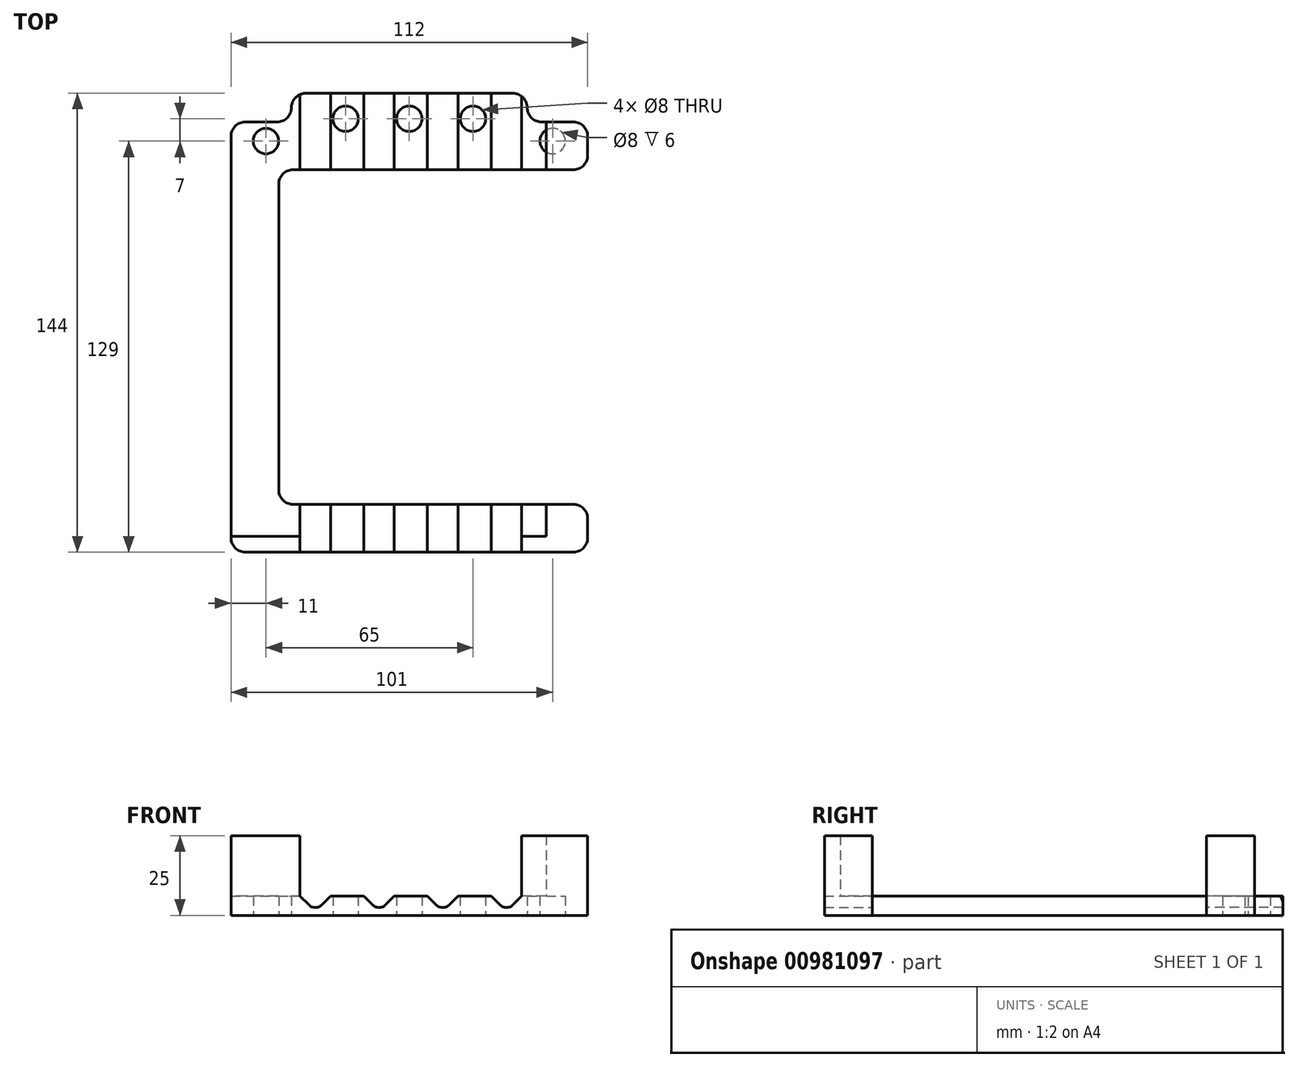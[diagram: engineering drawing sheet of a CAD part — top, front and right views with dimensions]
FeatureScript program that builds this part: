
annotation { "Feature Type Name" : "Feature", "Feature Type Description" : "" }
export const myFeature = defineFeature(function(context is Context, id is Id, definition is map)
    precondition{}
    {
        {
            var Q0;
            Q0=qCreatedBy(makeId("Top.planeOp"),FACE);
            var sketch = newSketch(context, id + "F0", { "sketchPlane" : qUnion([Q0])});
            skCircle(sketch, "E0", {"center": v(76, 136) * mm, "radius": 4 * mm});
            skLineSegment(sketch, "E1", {"start": v(88.5, 144) * mm, "end": v(23.5, 144) * mm});
            skLineSegment(sketch, "E2", {"start": v(19, 139.5) * mm, "end": v(19, 139.5) * mm});
            skLineSegment(sketch, "E3", {"start": v(14.5, 135) * mm, "end": v(4.5, 135) * mm});
            skLineSegment(sketch, "E4", {"start": v(0, 130.5) * mm, "end": v(0, 4.5) * mm});
            skLineSegment(sketch, "E5", {"start": v(4.5, 0) * mm, "end": v(107.5, 0) * mm});
            skLineSegment(sketch, "E6", {"start": v(112, 4.5) * mm, "end": v(112, 10.5) * mm});
            skLineSegment(sketch, "E7", {"start": v(107.5, 15) * mm, "end": v(19.5, 15) * mm});
            skLineSegment(sketch, "E8", {"start": v(107.5, 135) * mm, "end": v(97.5, 135) * mm});
            skLineSegment(sketch, "E9", {"start": v(93, 139.5) * mm, "end": v(93, 139.5) * mm});
            skLineSegment(sketch, "E10", {"start": v(112, 130.5) * mm, "end": v(112, 124.5) * mm});
            skLineSegment(sketch, "E11", {"start": v(107.5, 120) * mm, "end": v(19.5, 120) * mm});
            skCircle(sketch, "E12", {"center": v(56, 136) * mm, "radius": 4 * mm});
            skCircle(sketch, "E13", {"center": v(36, 136) * mm, "radius": 4 * mm});
            skCircle(sketch, "E14", {"center": v(11, 129) * mm, "radius": 4 * mm});
            skCircle(sketch, "E15", {"center": v(101, 129) * mm, "radius": 4 * mm});
            skLineSegment(sketch, "E16", {"start": v(15, 19.5) * mm, "end": v(15, 115.5) * mm});
            skPoint(sketch, "E17.visualSharp", {"position": v(19, 144) * mm});
            skArc(sketch, "E17.filletArc", {"start": v(23.5, 144) * mm, "mid": v(20.32, 142.68) * mm, "end": v(19, 139.5) * mm});
            skPoint(sketch, "E18.visualSharp", {"position": v(19, 135) * mm});
            skArc(sketch, "E18.filletArc", {"start": v(14.5, 135) * mm, "mid": v(17.68, 136.32) * mm, "end": v(19, 139.5) * mm});
            skPoint(sketch, "E19.visualSharp", {"position": v(93, 144) * mm});
            skArc(sketch, "E19.filletArc", {"start": v(93, 139.5) * mm, "mid": v(91.68, 142.68) * mm, "end": v(88.5, 144) * mm});
            skPoint(sketch, "E20.visualSharp", {"position": v(93, 135) * mm});
            skArc(sketch, "E20.filletArc", {"start": v(93, 139.5) * mm, "mid": v(94.32, 136.32) * mm, "end": v(97.5, 135) * mm});
            skPoint(sketch, "E21.visualSharp", {"position": v(112, 135) * mm});
            skArc(sketch, "E21.filletArc", {"start": v(112, 130.5) * mm, "mid": v(110.68, 133.68) * mm, "end": v(107.5, 135) * mm});
            skPoint(sketch, "E22.visualSharp", {"position": v(0, 135) * mm});
            skArc(sketch, "E22.filletArc", {"start": v(4.5, 135) * mm, "mid": v(1.32, 133.68) * mm, "end": v(0, 130.5) * mm});
            skPoint(sketch, "E23.visualSharp", {"position": v(15, 120) * mm});
            skArc(sketch, "E23.filletArc", {"start": v(19.5, 120) * mm, "mid": v(16.32, 118.68) * mm, "end": v(15, 115.5) * mm});
            skPoint(sketch, "E24.visualSharp", {"position": v(15, 15) * mm});
            skArc(sketch, "E24.filletArc", {"start": v(15, 19.5) * mm, "mid": v(16.32, 16.32) * mm, "end": v(19.5, 15) * mm});
            skPoint(sketch, "E25.visualSharp", {"position": v(0, 0) * mm});
            skArc(sketch, "E25.filletArc", {"start": v(0, 4.5) * mm, "mid": v(1.32, 1.32) * mm, "end": v(4.5, 0) * mm});
            skPoint(sketch, "E26.visualSharp", {"position": v(112, 0) * mm});
            skArc(sketch, "E26.filletArc", {"start": v(107.5, 0) * mm, "mid": v(110.68, 1.32) * mm, "end": v(112, 4.5) * mm});
            skPoint(sketch, "E27.visualSharp", {"position": v(112, 15) * mm});
            skArc(sketch, "E27.filletArc", {"start": v(112, 10.5) * mm, "mid": v(110.68, 13.68) * mm, "end": v(107.5, 15) * mm});
            skPoint(sketch, "E28.visualSharp", {"position": v(112, 120) * mm});
            skArc(sketch, "E28.filletArc", {"start": v(107.5, 120) * mm, "mid": v(110.68, 121.32) * mm, "end": v(112, 124.5) * mm});
            skSolve(sketch);
        }
        {
            var Q0;
            Q0 = qSketchRegion(id + "F0", true);
            extrude(context, id + "F1", {"entities" : qUnion([Q0]), "depth" : 6 * mm, "offsetDistance" : 25 * mm});
        }
        {
            var Q0;
            Q0=makeQuery(id+"F1.opExtrude","SWEPT_FACE",FACE,{"disambiguationData":[OSD([sQuery(id+"F0.wireOp",EDGE,"E11")])]});
            var sketch = newSketch(context, id + "F2", { "sketchPlane" : qUnion([Q0])});
            skLineSegment(sketch, "E29", {"start": v(21.7, 6) * mm, "end": v(24.38, 3.32) * mm});
            skLineSegment(sketch, "E30", {"start": v(28.62, 3.32) * mm, "end": v(31.3, 6) * mm});
            skLineSegment(sketch, "E31", {"start": v(31.3, 6) * mm, "end": v(41.7, 6) * mm});
            skLineSegment(sketch, "E32", {"start": v(41.7, 6) * mm, "end": v(44.38, 3.32) * mm});
            skLineSegment(sketch, "E33", {"start": v(48.62, 3.32) * mm, "end": v(51.3, 6) * mm});
            skLineSegment(sketch, "E34", {"start": v(51.3, 6) * mm, "end": v(61.7, 6) * mm});
            skLineSegment(sketch, "E35", {"start": v(61.7, 6) * mm, "end": v(64.38, 3.32) * mm});
            skLineSegment(sketch, "E36", {"start": v(68.62, 3.32) * mm, "end": v(71.3, 6) * mm});
            skLineSegment(sketch, "E37", {"start": v(71.3, 6) * mm, "end": v(81.7, 6) * mm});
            skLineSegment(sketch, "E38", {"start": v(81.7, 6) * mm, "end": v(84.38, 3.32) * mm});
            skLineSegment(sketch, "E39", {"start": v(88.62, 3.32) * mm, "end": v(91.3, 6) * mm});
            skLineSegment(sketch, "E40", {"start": v(91.3, 6) * mm, "end": v(91.3, 7) * mm});
            skLineSegment(sketch, "E41", {"start": v(91.3, 7) * mm, "end": v(21.7, 7) * mm});
            skLineSegment(sketch, "E42", {"start": v(21.7, 7) * mm, "end": v(21.7, 6) * mm});
            skPoint(sketch, "E43.visualSharp", {"position": v(86.5, 1.2) * mm});
            skArc(sketch, "E43.filletArc", {"start": v(84.38, 3.32) * mm, "mid": v(86.5, 2.44) * mm, "end": v(88.62, 3.32) * mm});
            skPoint(sketch, "E44.visualSharp", {"position": v(66.5, 1.2) * mm});
            skArc(sketch, "E44.filletArc", {"start": v(64.38, 3.32) * mm, "mid": v(66.5, 2.44) * mm, "end": v(68.62, 3.32) * mm});
            skPoint(sketch, "E45.visualSharp", {"position": v(46.5, 1.2) * mm});
            skArc(sketch, "E45.filletArc", {"start": v(44.38, 3.32) * mm, "mid": v(46.5, 2.44) * mm, "end": v(48.62, 3.32) * mm});
            skPoint(sketch, "E46.visualSharp", {"position": v(26.5, 1.2) * mm});
            skArc(sketch, "E46.filletArc", {"start": v(24.38, 3.32) * mm, "mid": v(26.5, 2.44) * mm, "end": v(28.62, 3.32) * mm});
            skSolve(sketch);
        }
        {
            var Q0;
            Q0 = qSketchRegion(id + "F2", true);
            extrude(context, id + "F3", {"entities" : qUnion([Q0]), "operationType" : NewBodyOperationType.REMOVE, "oppositeDirection" : true, "depth" : 25 * mm, "offsetDistance" : 25 * mm});
        }
        {
            var Q0;
            Q0 = qSketchRegion(id + "F2", true);
            extrude(context, id + "F4", {"entities" : qUnion([Q0]), "operationType" : NewBodyOperationType.REMOVE, "endBound" : BoundingType.THROUGH_ALL, "depth" : 25 * mm, "offsetDistance" : 25 * mm});
        }
        {
            var Q0;
            {var subQ0=sQuery(id+"F0.wireOp",EDGE,"E18.filletArc");var subQ2=sQuery(id+"F0.wireOp",EDGE,"E14");var subQ4=sQuery(id+"F0.wireOp",EDGE,"E22.filletArc");var subQ7=sQuery(id+"F0.wireOp",EDGE,"E11");var subQ9=sQuery(id+"F0.wireOp",EDGE,"E3");var subQ10=makeQuery(id+"F1.opExtrude","SWEPT_FACE",FACE,{"disambiguationData":[OSD([subQ9])]});var subQ11=sQuery(id+"F0.wireOp",EDGE,"E16");var subQ13=sQuery(id+"F0.wireOp",EDGE,"E4");var subQ15=sQuery(id+"F0.wireOp",EDGE,"E17.filletArc");var subQ17=sQuery(id+"F0.wireOp",EDGE,"E5");var subQ19=sQuery(id+"F0.wireOp",EDGE,"E7");var subQ21=sQuery(id+"F0.wireOp",EDGE,"E23.filletArc");var subQ23=sQuery(id+"F0.wireOp",EDGE,"E24.filletArc");var subQ25=sQuery(id+"F0.wireOp",EDGE,"E25.filletArc");var subQ28=sQuery(id+"F0.wireOp",EDGE,"E27.filletArc");var subQ29=sQuery(id+"F0.wireOp",EDGE,"E6");var subQ30=sQuery(id+"F0.wireOp",EDGE,"E26.filletArc");Q0=makeQuery(id+"F4.boolean.opBoolean","SPLIT",FACE,{"disambiguationData":[TD([subQ10])],"derivedFrom":makeQuery(id+"F3.boolean.opBoolean","SPLIT",FACE,{"disambiguationData":[TD([subQ10])],"derivedFrom":makeQuery(id+"F1.opExtrude","CAP_FACE",FACE,{"disambiguationData":[OSD([sQuery(id+"F0.wireOp",EDGE,"E0"),sQuery(id+"F0.wireOp",EDGE,"E1"),subQ9,subQ13,subQ17,subQ29,subQ19,sQuery(id+"F0.wireOp",EDGE,"E8"),sQuery(id+"F0.wireOp",EDGE,"E10"),subQ7,sQuery(id+"F0.wireOp",EDGE,"E12"),sQuery(id+"F0.wireOp",EDGE,"E13"),subQ2,sQuery(id+"F0.wireOp",EDGE,"E15"),subQ11,subQ15,subQ0,sQuery(id+"F0.wireOp",EDGE,"E19.filletArc"),sQuery(id+"F0.wireOp",EDGE,"E20.filletArc"),sQuery(id+"F0.wireOp",EDGE,"E21.filletArc"),subQ4,subQ21,subQ23,subQ25,subQ30,subQ28,sQuery(id+"F0.wireOp",EDGE,"E28.filletArc")])],"isStart":false})})});}
            var sketch = newSketch(context, id + "F5", { "sketchPlane" : qUnion([Q0])});
            skLineSegment(sketch, "E47.bottom", {"start": v(0, 5) * mm, "end": v(21.7, 5) * mm});
            skLineSegment(sketch, "E47.top", {"start": v(4.5, 0) * mm, "end": v(21.7, 0) * mm});
            skLineSegment(sketch, "E47.left", {"start": v(0, 5) * mm, "end": v(0, 4.5) * mm});
            skLineSegment(sketch, "E47.right", {"start": v(21.7, 5) * mm, "end": v(21.7, 0) * mm});
            skLineSegment(sketch, "E48", {"start": v(91.3, 0) * mm, "end": v(107.5, 0) * mm});
            skLineSegment(sketch, "E49", {"start": v(112, 4.5) * mm, "end": v(112, 10.5) * mm});
            skLineSegment(sketch, "E50", {"start": v(107.5, 15) * mm, "end": v(99, 15) * mm});
            skLineSegment(sketch, "E51", {"start": v(99, 15) * mm, "end": v(99, 5) * mm});
            skLineSegment(sketch, "E52", {"start": v(99, 5) * mm, "end": v(91.3, 5) * mm});
            skLineSegment(sketch, "E53", {"start": v(91.3, 5) * mm, "end": v(91.3, 0) * mm});
            skLineSegment(sketch, "E54.bottom", {"start": v(99, 135) * mm, "end": v(107.5, 135) * mm});
            skLineSegment(sketch, "E54.top", {"start": v(99, 120) * mm, "end": v(107.5, 120) * mm});
            skLineSegment(sketch, "E54.left", {"start": v(99, 135) * mm, "end": v(99, 120) * mm});
            skLineSegment(sketch, "E54.right", {"start": v(112, 130.5) * mm, "end": v(112, 124.5) * mm});
            skPoint(sketch, "E55.visualSharp", {"position": v(112, 135) * mm});
            skArc(sketch, "E55.filletArc", {"start": v(112, 130.5) * mm, "mid": v(110.68, 133.68) * mm, "end": v(107.5, 135) * mm});
            skPoint(sketch, "E56.visualSharp", {"position": v(112, 120) * mm});
            skArc(sketch, "E56.filletArc", {"start": v(107.5, 120) * mm, "mid": v(110.68, 121.32) * mm, "end": v(112, 124.5) * mm});
            skPoint(sketch, "E57.visualSharp", {"position": v(112, 15) * mm});
            skArc(sketch, "E57.filletArc", {"start": v(112, 10.5) * mm, "mid": v(110.68, 13.68) * mm, "end": v(107.5, 15) * mm});
            skPoint(sketch, "E58.visualSharp", {"position": v(112, 0) * mm});
            skArc(sketch, "E58.filletArc", {"start": v(107.5, 0) * mm, "mid": v(110.68, 1.32) * mm, "end": v(112, 4.5) * mm});
            skPoint(sketch, "E59.visualSharp", {"position": v(0, 0) * mm});
            skArc(sketch, "E59.filletArc", {"start": v(0, 4.5) * mm, "mid": v(1.32, 1.32) * mm, "end": v(4.5, 0) * mm});
            skSolve(sketch);
        }
        {
            var Q0;
            Q0 = qSketchRegion(id + "F5", true);
            extrude(context, id + "F6", {"entities" : qUnion([Q0]), "operationType" : NewBodyOperationType.ADD, "depth" : 19 * mm, "offsetDistance" : 25 * mm});
        }
    });
